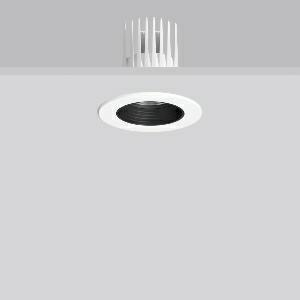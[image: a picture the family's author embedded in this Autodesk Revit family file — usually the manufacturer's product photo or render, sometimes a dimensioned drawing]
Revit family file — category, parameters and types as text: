
# Revit family: heledon_mini_e_901753_002_3_7dfc
name_source: partatom
category: Lighting Fixtures
units: mm (PartAtom-declared; Revit-internal decimal feet)

## family parameters
Cut with Voids When Loaded = No
Host = Face
Light Source = No
Part Type = Normal
Room Calculation Point = No
Round Connector Dimension = Use Diameter
Shared = No

## types (1)
- HELEDON mini E (1 x LED Modul 935, 2900 lm, 3500)
    Apparent Load = 29 VA
    Approval mark = CE
    CIE Flux Codes = 98 100 100 100 100
    Color Rendering = 92
    Color Temperature = 3500
    Default Elevation = 1800 mm
    Description = Series: HELEDON mini
Round recessed downlight. Housing: die-cast aluminium, powder-coated. Black plastic ring and recessed LED to prevent glare from the side. Optical assembly with lens made of plastic (polycarbonate) for the best homogeneous light distribution - can be changed without tools. Best colour rendering index Ra>90. Suitable for Recessed ceiling mounting. Installation without tools thanks to spring fastening system. Including separate LED converter with connecting cable 600 mm.High quality converter without flickering and stroboscopic effect. Through-wiring box (5 pole) available as accessory. The following accessories can be mounted without use of tools: interchangeable lenses, decorative glasses, honeycomb louvre, clear and frosted diffusers, white interchangeable plastic ring. 
Colour: traffic white, matt (RAL 9016)
Diameter: 124 mm
Height: 3 mm
Cut-out diameter: 114 mm
Recess height: 170 mm
Luminaire: recess height: 120 mm
Lamp: LED
Socket: without socket
Colour temperature: 3500K
Colour rendering index (CRI): 92
System power: 29 W
Rated luminous flux: 2900 lm
Luminous efficiency: 100 lm/W
Control gear: Regulated power supply
Protection class: II
Type of protection: IP 20
    Height = 0 mm  [stored 0 ft]
    Lamp = 1 x LED Modul 935
    Lamp Light Flux = 2900 lm
    Lamp count = 1
    Length = 124 mm  [stored 0.406824 ft]
    Lifetime = 50000 h
    Luminous efficacy = 100 lm/W
    Manufacturer = RZB
    ModVariant = No
    Model = 901753.002.3
    Mounting Place = Ceiling
    Mounting Type = Recessed
    Number of Poles = 1
    OnlyDefault = Yes
    Power Factor = 1
    Product Name = HELEDON mini E
    Product group = Recessed downlights
    ProductGroupID = 402
    Protection Class = Protection class II
    Protection Degree = IP 20
    RLX_Detail_Level = 1
    RLX_Emergency_Light_Flux = 0 lm
    RLX_Emergency_Type = 0
    RLX_Emergency_Type_DB = No
    RlxData = <blob elided: 128393 chars, md5=cf6aeeba>
    Socket = socket
    Standby Power = 0 W
    System Light Flux = 2900 lm
    System Power = 29 W
    Type Comments = Product without accessories
    Type Image = 901656.002.jpg
    URL = http://relux.com
    VarID = ---
    Voltage = 230 V
    Voltage Range = 220-240 V
    Weight = 0.00 kg
    Width = 0 mm  [stored 0 ft]

note: [stored X ft] marks values corroborated as IEEE doubles in the binary element streams (Revit-internal decimal feet)

## geometry (parser evidence)
native form markers: Blend x4, Sweep x12
no freeform markers — native parametric forms only
